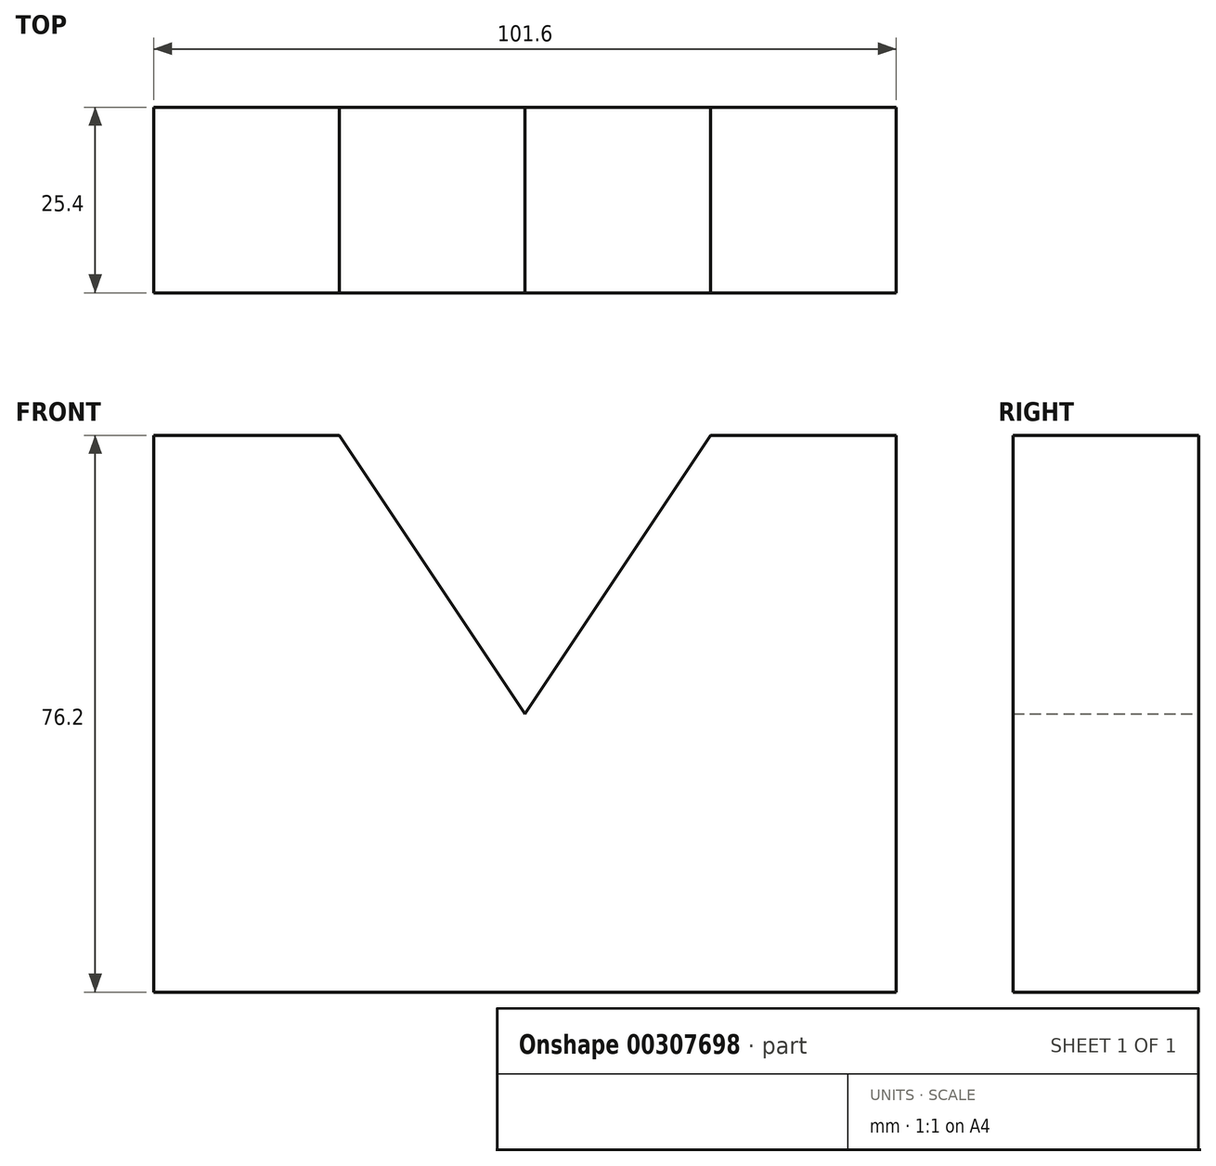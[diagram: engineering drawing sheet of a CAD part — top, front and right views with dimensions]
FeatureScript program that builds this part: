
annotation { "Feature Type Name" : "Feature", "Feature Type Description" : "" }
export const myFeature = defineFeature(function(context is Context, id is Id, definition is map)
    precondition{}
    {
        {
            var Q0;
            Q0=qCreatedBy(makeId("Front.planeOp"),FACE);
            var sketch = newSketch(context, id + "F0", { "sketchPlane" : qUnion([Q0])});
            skLineSegment(sketch, "E0", {"start": v(-62.51, -35.76) * mm, "end": v(39.09, -35.76) * mm});
            skLineSegment(sketch, "E1", {"start": v(39.09, -35.76) * mm, "end": v(39.09, 40.44) * mm});
            skLineSegment(sketch, "E2", {"start": v(39.09, 40.44) * mm, "end": v(13.69, 40.44) * mm});
            skLineSegment(sketch, "E3", {"start": v(-37.11, 40.44) * mm, "end": v(-62.51, 40.44) * mm});
            skLineSegment(sketch, "E4", {"start": v(-62.51, 40.44) * mm, "end": v(-62.51, -35.76) * mm});
            skLineSegment(sketch, "E5", {"start": v(-11.71, 2.34) * mm, "end": v(-37.11, 40.44) * mm});
            skPoint(sketch, "E5.startSnap0", {"position": v(-11.71, -35.76) * mm});
            skLineSegment(sketch, "E6", {"start": v(-11.71, 2.34) * mm, "end": v(13.69, 40.44) * mm});
            skSolve(sketch);
        }
        {
            var Q0;
            Q0=makeQuery(id+"F0.imprint","IMPRINT",FACE,{"disambiguationData":[TD([[makeQuery(id+"F0.imprint","IMPRINT",EDGE,{"derivedFrom":sQuery(id+"F0.wireOp",EDGE,"E0")}),1.0]])]});
            extrude(context, id + "F1", {"entities" : qUnion([Q0]), "depth" : 25.4 * mm});
        }
    });
